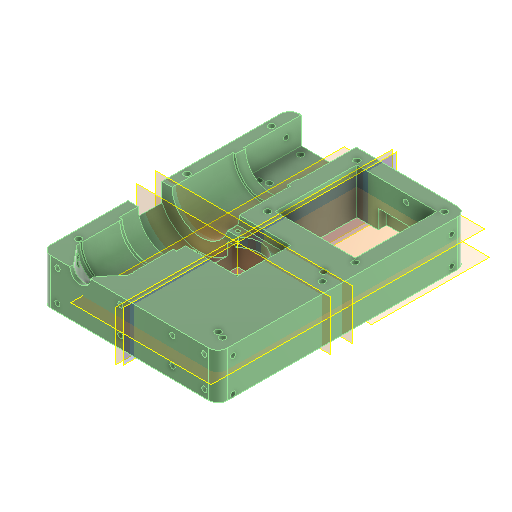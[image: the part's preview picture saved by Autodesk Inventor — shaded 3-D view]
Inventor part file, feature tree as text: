
AUTODESK INVENTOR PART (.ipt)
format: ipt  version: 2024.1 (Build 281209000, 209)  size: 666,624 bytes
history: native  units: mm
features: reference x15, sketch x10, plane x7, other x6, projected_geometry x6, extrude x5, hole x4, mirror x2, revolve x1, fillet x1
ambient origin geometry x8: Origin, YZ Plane, XZ Plane, XY Plane, X Axis, Y Axis, Z Axis, Center Point
bodies: Volumenkörper1 (feature_tree)
feature tree (57):
  plane  "Arbeitsebene1"
  plane  "Arbeitsebene2"
  extrude  "Extrusion1"  Depth=2.8mm
  revolve  "Umdrehung1"
  extrude  "Extrusion4"  Depth=2.8mm
  hole  "Bohrung1"  [1 undecoded]
  hole  "Bohrung2"  [1 undecoded]
  extrude  "Extrusion7"  TaperAngle=360.0deg  [1 undecoded]
  fillet  "Rundung2"  Radius=0.3mm
  hole  "Bohrung6"  [1 undecoded]
  other  "Arbeitsachse1"
  plane  "Arbeitsebene5"
  extrude  "Extrusion8"  Depth=31.15mm
  extrude  "Extrusion9"  Depth=1.0mm
  plane  "Arbeitsebene6"
  mirror  "Spiegeln1"
  plane  "Arbeitsebene7"
  mirror  "Spiegeln2"
  hole  "Bohrung7"  [1 undecoded]
  sketch  "Skizze1"  dims[d0=0.5mm d1=2.8mm]
  sketch  "Skizze2"  dims[d2=2.8mm d3=2.8mm]
  projected_geometry  "Projizierte Kontur1"
  sketch  "Skizze5"  dims[d4=2.8mm d5=95.0mm]
  projected_geometry  "Projizierte Kontur2"
  reference  "Referenz19"
  reference  "Referenz20"
  sketch  "Skizze6"  dims[d6=132.0mm d7=50.0mm d8=0.0mm]
  projected_geometry  "Projizierte Kontur3"
  sketch  "Skizze8"  dims[d9=0.25mm d10=360.0deg d23=0.3mm]
  projected_geometry  "Projizierte Kontur4"
  sketch  "Skizze13"  dims[d24=14.3mm d25=0.0mm d26=10.0mm]
  projected_geometry  "Projizierte Kontur8"
  sketch  "Skizze14"  dims[d27=3.3mm d28=6.0mm d29=4.0mm d30=8.0mm d31=90.0deg d32=8.0mm d33=20.594885mm d41=31.15mm]
  plane  "Arbeitsebene3"
  plane  "Arbeitsebene4"
  sketch  "Skizze15"  dims[d43=2.8mm d44=6.0mm d45=6.5mm d46=8.0mm d47=90.0deg d48=12.0mm d49=20.594885mm d74=1.0mm]
  reference  "Referenz28"
  reference  "Referenz29"
  reference  "Referenz30"
  reference  "Referenz31"
  reference  "Referenz32"
  reference  "Referenz33"
  projected_geometry  "Projizierte Kontur9"
  reference  "Referenz34"
  reference  "Referenz35"
  reference  "Referenz36"
  reference  "Referenz37"
  sketch  "Skizze16"  dims[d75=2.25mm d80=20.0mm]
  reference  "Referenz39"
  sketch  "Skizze17"  dims[d81=9.0mm d82=10.0mm d83=0.0mm d84=5.0mm d85=2.8mm d86=6.0mm d87=4.0mm d88=2.0mm d89=90.0deg d90=12.0mm d91=20.594885mm d92=28.5mm d93=28.5mm d96=-10.0mm d97=25.0mm d98=5.0mm d99=0.0mm d101=45.0mm d102=18.0mm d103=0.0mm d104=15.4mm d105=55.0mm d107=43.3mm d108=43.0mm d109=2.0mm d110=2.0mm d111=2.0mm d112=2.0mm d113=2.0mm d114=2.0mm d115=2.0mm d116=2.0mm d117=8.0mm d118=8.0mm d119=16.3mm d120=116.0mm d121=5.0mm d122=3.3mm d123=6.0mm d124=7.0mm d125=3.0mm d126=90.0deg d127=8.0mm d128=20.594885mm]
  reference  "Referenz40"
  reference  "Referenz41"
  other  "Assembly_Planktoscope_Uc2version_wormdrive_V3.iam"
  other  "00_HIKCamera_MV-CE060-10UMUC:1"
  other  "00_NEMA11:1"
  other  "00_10x_Objective_ViewSolutions_bm05073332:2"
  other  "00_NEMA17_Perestalticpump_Adapter:1"
note: 5 required parameter values undecoded (feature->parameter linkage not recoverable at this tier; creation-order binding heuristic only, values carry confidence <= 0.55)
